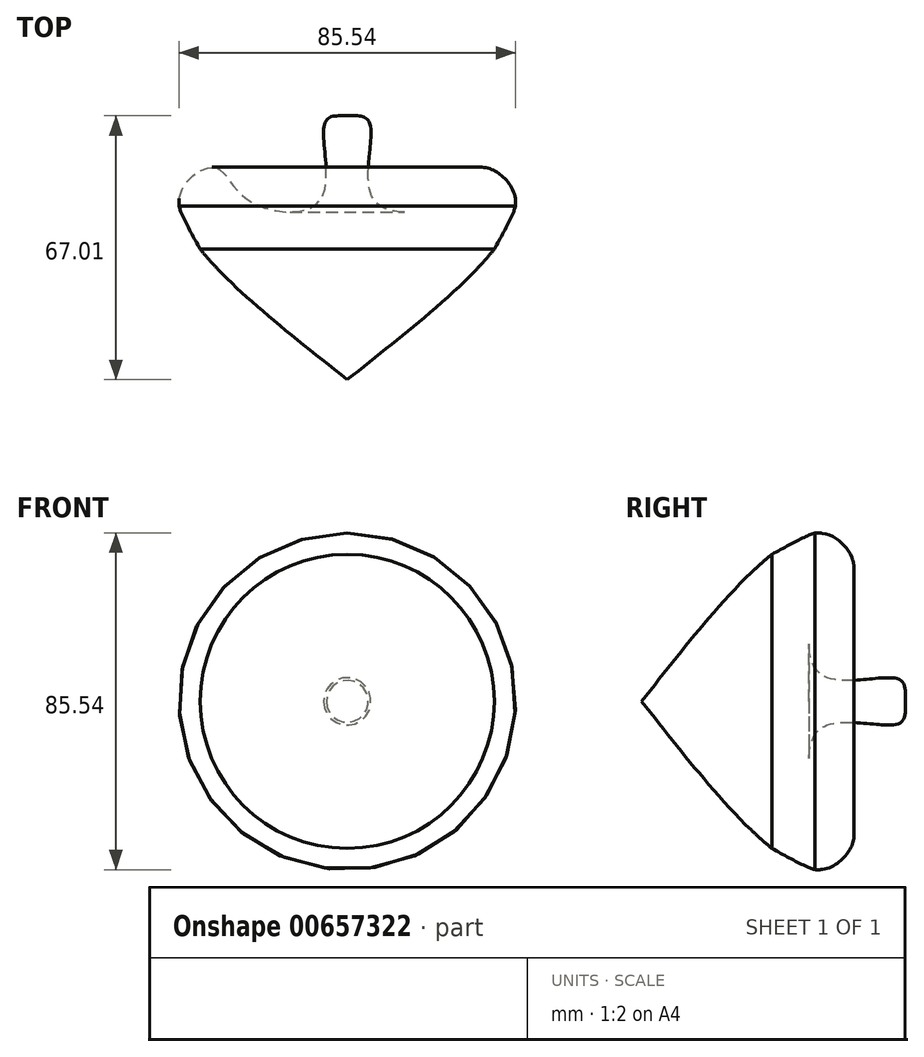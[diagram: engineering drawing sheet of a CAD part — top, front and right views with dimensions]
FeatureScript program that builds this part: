
annotation { "Feature Type Name" : "Feature", "Feature Type Description" : "" }
export const myFeature = defineFeature(function(context is Context, id is Id, definition is map)
    precondition{}
    {
        {
            var Q0;
            Q0=qCreatedBy(makeId("Top.planeOp"),FACE);
            var sketch = newSketch(context, id + "F0", { "sketchPlane" : qUnion([Q0])});
            skLineSegment(sketch, "E0", {"start": v(0, 74.67) * mm, "end": v(0, -77.17) * mm});
            skFitSpline(sketch, "E1", {"points": [v(0, -77.17) * mm, v(-42.69, -31.18) * mm, v(-33.62, -23.3) * mm, v(-25.74, -31.18) * mm, v(-6.82, -31.58) * mm, v(-5.64, -11.87) * mm, v(0, -10.3) * mm], "startDerivative": vector(-217.7, 171.6) * mm, "endDerivative": vector(77.37, -6.92) * mm});
            skFitSpline(sketch, "E2", {"points": [v(-37.35, -44.03) * mm, v(-42.69, -31.18) * mm, v(-32.84, -35.13) * mm], "startDerivative": vector(-18.31, 32.74) * mm, "endDerivative": vector(28.4, -16.03) * mm});
            skFitSpline(sketch, "E3", {"points": [v(-32.72, -49.3) * mm, v(-25.74, -44.03) * mm], "startDerivative": vector(6.98, 5.28) * mm, "endDerivative": vector(6.98, 5.28) * mm});
            skSolve(sketch);
        }
        {
            var Q0;
            {var subQ1=sQuery(id+"F0.wireOp",EDGE,"E1");var subQ5=makeQuery(id+"F0.imprint","IMPRINT",VERTEX,{"derivedFrom":subQ1});Q0=makeQuery(id+"F0.imprint","IMPRINT",FACE,{"disambiguationData":[TD([[makeQuery(id+"F0.imprint","IMPRINT",EDGE,{"disambiguationData":[TD([[subQ5,1.0]])],"derivedFrom":subQ1}),-1.0]])]});}
            var Q1;
            Q1=sQuery(id+"F0.wireOp",EDGE,"E0");
            revolve(context, id + "F1", {"entities" : qUnion([Q0]), "axis" : qUnion([Q1]), "revolveType" : RevolveType.FULL});
        }
    });
